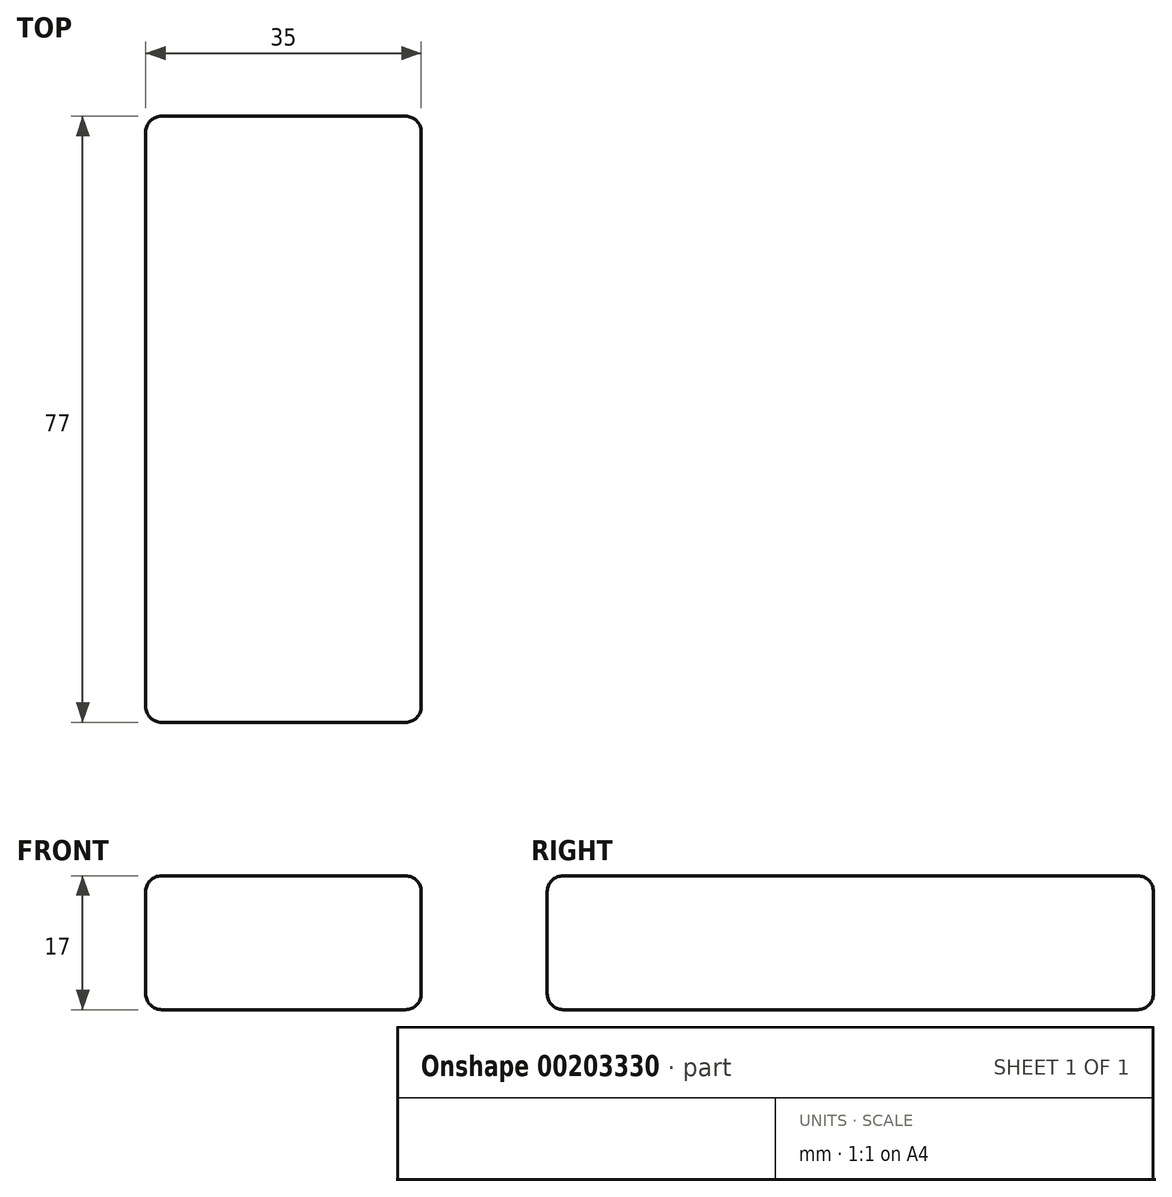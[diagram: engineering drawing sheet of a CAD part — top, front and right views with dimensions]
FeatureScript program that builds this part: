
annotation { "Feature Type Name" : "Feature", "Feature Type Description" : "" }
export const myFeature = defineFeature(function(context is Context, id is Id, definition is map)
    precondition{}
    {
        {
            var Q0;
            Q0=qCreatedBy(makeId("Top.planeOp"),FACE);
            var sketch = newSketch(context, id + "F0", { "sketchPlane" : qUnion([Q0])});
            skLineSegment(sketch, "E0.bottom", {"start": v(17.5, -38.5) * mm, "end": v(-17.5, -38.5) * mm});
            skLineSegment(sketch, "E0.top", {"start": v(17.5, 38.5) * mm, "end": v(-17.5, 38.5) * mm});
            skLineSegment(sketch, "E0.left", {"start": v(17.5, -38.5) * mm, "end": v(17.5, 38.5) * mm});
            skLineSegment(sketch, "E0.right", {"start": v(-17.5, -38.5) * mm, "end": v(-17.5, 38.5) * mm});
            skPoint(sketch, "E0.middle", {"position": v(0, 0) * mm});
            skSolve(sketch);
        }
        {
            var Q0;
            Q0 = qSketchRegion(id + "F0", true);
            extrude(context, id + "F1", {"entities" : qUnion([Q0]), "endBound" : BoundingType.SYMMETRIC, "depth" : 17 * mm});
        }
        {
            var Q0;
            Q0=makeQuery(id+"F1.opExtrude","CAP_EDGE",EDGE,{"disambiguationData":[OSD([sQuery(id+"F0.wireOp",EDGE,"E0.top")])],"isStart":false});
            var Q1;
            Q1=makeQuery(id+"F1.opExtrude","SWEPT_EDGE",EDGE,{"disambiguationData":[OSD([sQuery(id+"F0.wireOp",EDGE,"E0.top"),sQuery(id+"F0.wireOp",EDGE,"E0.left")])]});
            var Q2;
            Q2=makeQuery(id+"F1.opExtrude","CAP_EDGE",EDGE,{"disambiguationData":[OSD([sQuery(id+"F0.wireOp",EDGE,"E0.top")])],"isStart":true});
            var Q3;
            Q3=makeQuery(id+"F1.opExtrude","SWEPT_EDGE",EDGE,{"disambiguationData":[OSD([sQuery(id+"F0.wireOp",EDGE,"E0.top"),sQuery(id+"F0.wireOp",EDGE,"E0.right")])]});
            var Q4;
            Q4=makeQuery(id+"F1.opExtrude","CAP_EDGE",EDGE,{"disambiguationData":[OSD([sQuery(id+"F0.wireOp",EDGE,"E0.left")])],"isStart":true});
            var Q5;
            Q5=makeQuery(id+"F1.opExtrude","CAP_EDGE",EDGE,{"disambiguationData":[OSD([sQuery(id+"F0.wireOp",EDGE,"E0.right")])],"isStart":true});
            var Q6;
            Q6=makeQuery(id+"F1.opExtrude","CAP_EDGE",EDGE,{"disambiguationData":[OSD([sQuery(id+"F0.wireOp",EDGE,"E0.bottom")])],"isStart":true});
            var Q7;
            Q7=makeQuery(id+"F1.opExtrude","CAP_EDGE",EDGE,{"disambiguationData":[OSD([sQuery(id+"F0.wireOp",EDGE,"E0.bottom")])],"isStart":false});
            var Q8;
            Q8=makeQuery(id+"F1.opExtrude","SWEPT_EDGE",EDGE,{"disambiguationData":[OSD([sQuery(id+"F0.wireOp",EDGE,"E0.bottom"),sQuery(id+"F0.wireOp",EDGE,"E0.right")])]});
            var Q9;
            Q9=makeQuery(id+"F1.opExtrude","SWEPT_EDGE",EDGE,{"disambiguationData":[OSD([sQuery(id+"F0.wireOp",EDGE,"E0.bottom"),sQuery(id+"F0.wireOp",EDGE,"E0.left")])]});
            var Q10;
            Q10=makeQuery(id+"F1.opExtrude","CAP_EDGE",EDGE,{"disambiguationData":[OSD([sQuery(id+"F0.wireOp",EDGE,"E0.right")])],"isStart":false});
            var Q11;
            Q11=makeQuery(id+"F1.opExtrude","CAP_EDGE",EDGE,{"disambiguationData":[OSD([sQuery(id+"F0.wireOp",EDGE,"E0.left")])],"isStart":false});
            fillet(context, id + "F2", {"entities" : qUnion([Q0, Q1, Q2, Q3, Q4, Q5, Q6, Q7, Q8, Q9, Q10, Q11]), "radius" : 2 * mm, "tangentPropagation" : true, "allowEdgeOverflow" : false});
        }
    });
